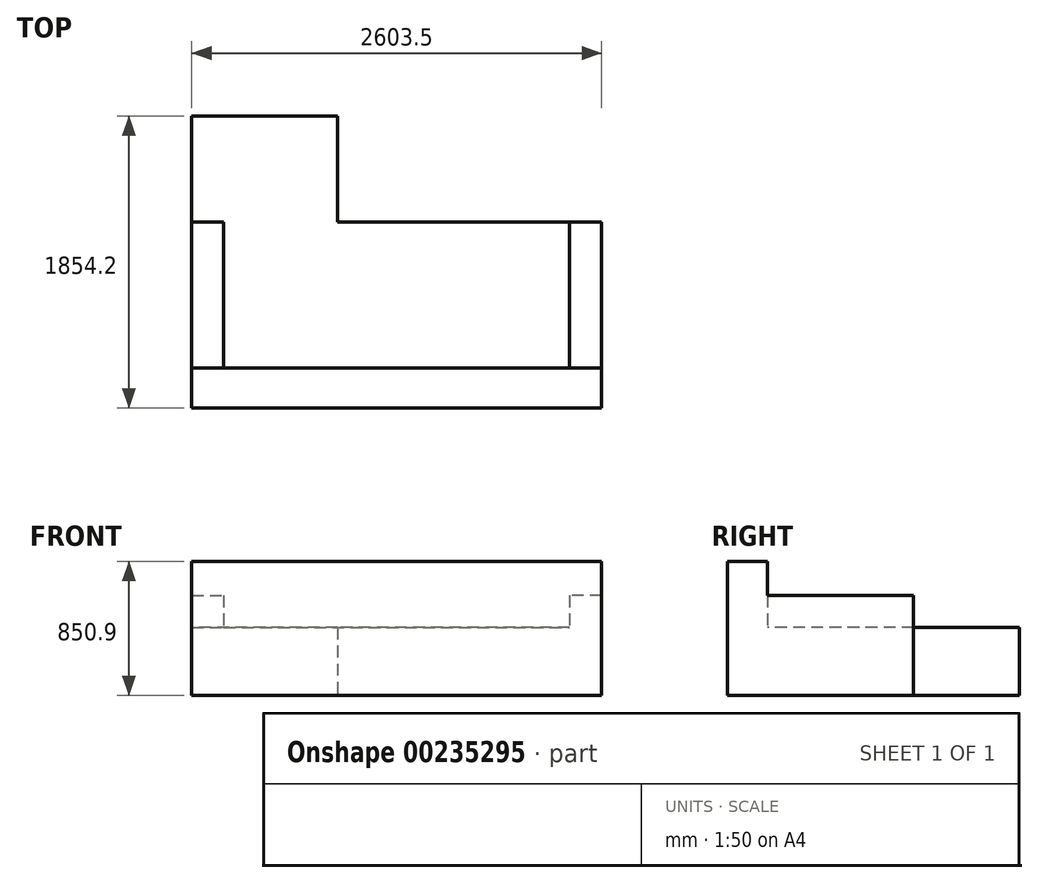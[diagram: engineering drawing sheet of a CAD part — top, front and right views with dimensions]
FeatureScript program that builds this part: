
annotation { "Feature Type Name" : "Feature", "Feature Type Description" : "" }
export const myFeature = defineFeature(function(context is Context, id is Id, definition is map)
    precondition{}
    {
        {
            var Q0;
            Q0=qCreatedBy(makeId("Top.planeOp"),FACE);
            var sketch = newSketch(context, id + "F0", { "sketchPlane" : qUnion([Q0])});
            skLineSegment(sketch, "E0", {"start": v(-1301.75, 1263.65) * mm, "end": v(-1301.75, -590.55) * mm});
            skLineSegment(sketch, "E1", {"start": v(-1301.75, -590.55) * mm, "end": v(1301.75, -590.55) * mm});
            skLineSegment(sketch, "E2", {"start": v(1301.75, -590.55) * mm, "end": v(1301.75, 590.55) * mm});
            skLineSegment(sketch, "E3", {"start": v(1301.75, 590.55) * mm, "end": v(-374.65, 590.55) * mm});
            skLineSegment(sketch, "E4", {"start": v(-374.65, 590.55) * mm, "end": v(-374.65, 1263.65) * mm});
            skLineSegment(sketch, "E5", {"start": v(-374.65, 1263.65) * mm, "end": v(-1301.75, 1263.65) * mm});
            skLineSegment(sketch, "E6", {"start": v(1301.75, 0) * mm, "end": v(-1301.75, 0) * mm, "construction": true});
            skSolve(sketch);
        }
        {
            var Q0;
            Q0 = qSketchRegion(id + "F0", true);
            extrude(context, id + "F1", {"entities" : qUnion([Q0]), "depth" : 431.8 * mm});
        }
        {
            var Q0;
            Q0=makeQuery(id+"F1.opExtrude","CAP_FACE",FACE,{"disambiguationData":[OSD([sQuery(id+"F0.wireOp",EDGE,"E0"),sQuery(id+"F0.wireOp",EDGE,"E1"),sQuery(id+"F0.wireOp",EDGE,"E2"),sQuery(id+"F0.wireOp",EDGE,"E3"),sQuery(id+"F0.wireOp",EDGE,"E4"),sQuery(id+"F0.wireOp",EDGE,"E5")])],"isStart":false});
            var sketch = newSketch(context, id + "F2", { "sketchPlane" : qUnion([Q0])});
            skLineSegment(sketch, "E7.0", {"start": v(-1301.75, -336.55) * mm, "end": v(1301.75, -336.55) * mm});
            skLineSegment(sketch, "E8", {"start": v(-1047.75, 1263.65) * mm, "end": v(-1301.75, 1263.65) * mm});
            skLineSegment(sketch, "E9", {"start": v(1301.75, -336.55) * mm, "end": v(1301.75, -590.55) * mm});
            skLineSegment(sketch, "E10.1", {"start": v(-1301.75, -590.55) * mm, "end": v(1301.75, -590.55) * mm});
            skLineSegment(sketch, "E11", {"start": v(-1301.75, -336.55) * mm, "end": v(-1301.75, -590.55) * mm});
            skSolve(sketch);
        }
        {
            var Q0;
            Q0 = qSketchRegion(id + "F2", true);
            extrude(context, id + "F3", {"entities" : qUnion([Q0]), "operationType" : NewBodyOperationType.ADD, "depth" : 419.1 * mm});
        }
        {
            var Q0;
            Q0=makeQuery(id+"F1.opExtrude","CAP_FACE",FACE,{"disambiguationData":[OSD([sQuery(id+"F0.wireOp",EDGE,"E0"),sQuery(id+"F0.wireOp",EDGE,"E1"),sQuery(id+"F0.wireOp",EDGE,"E2"),sQuery(id+"F0.wireOp",EDGE,"E3"),sQuery(id+"F0.wireOp",EDGE,"E4"),sQuery(id+"F0.wireOp",EDGE,"E5")])],"isStart":false});
            var sketch = newSketch(context, id + "F4", { "sketchPlane" : qUnion([Q0])});
            skLineSegment(sketch, "E12.bottom", {"start": v(1301.75, 590.55) * mm, "end": v(1098.55, 590.55) * mm});
            skLineSegment(sketch, "E12.top", {"start": v(1301.75, -336.55) * mm, "end": v(1098.55, -336.55) * mm});
            skLineSegment(sketch, "E12.left", {"start": v(1301.75, 590.55) * mm, "end": v(1301.75, -336.55) * mm});
            skLineSegment(sketch, "E12.right", {"start": v(1098.55, 590.55) * mm, "end": v(1098.55, -336.55) * mm});
            skLineSegment(sketch, "E13.bottom", {"start": v(-1301.75, 590.55) * mm, "end": v(-1098.55, 590.55) * mm});
            skLineSegment(sketch, "E13.top", {"start": v(-1301.75, -336.55) * mm, "end": v(-1098.55, -336.55) * mm});
            skLineSegment(sketch, "E13.left", {"start": v(-1301.75, 590.55) * mm, "end": v(-1301.75, -336.55) * mm});
            skLineSegment(sketch, "E13.right", {"start": v(-1098.55, 590.55) * mm, "end": v(-1098.55, -336.55) * mm});
            skSolve(sketch);
        }
        {
            var Q0;
            Q0 = qSketchRegion(id + "F4", true);
            extrude(context, id + "F5", {"entities" : qUnion([Q0]), "operationType" : NewBodyOperationType.ADD, "depth" : 203.2 * mm});
        }
    });
